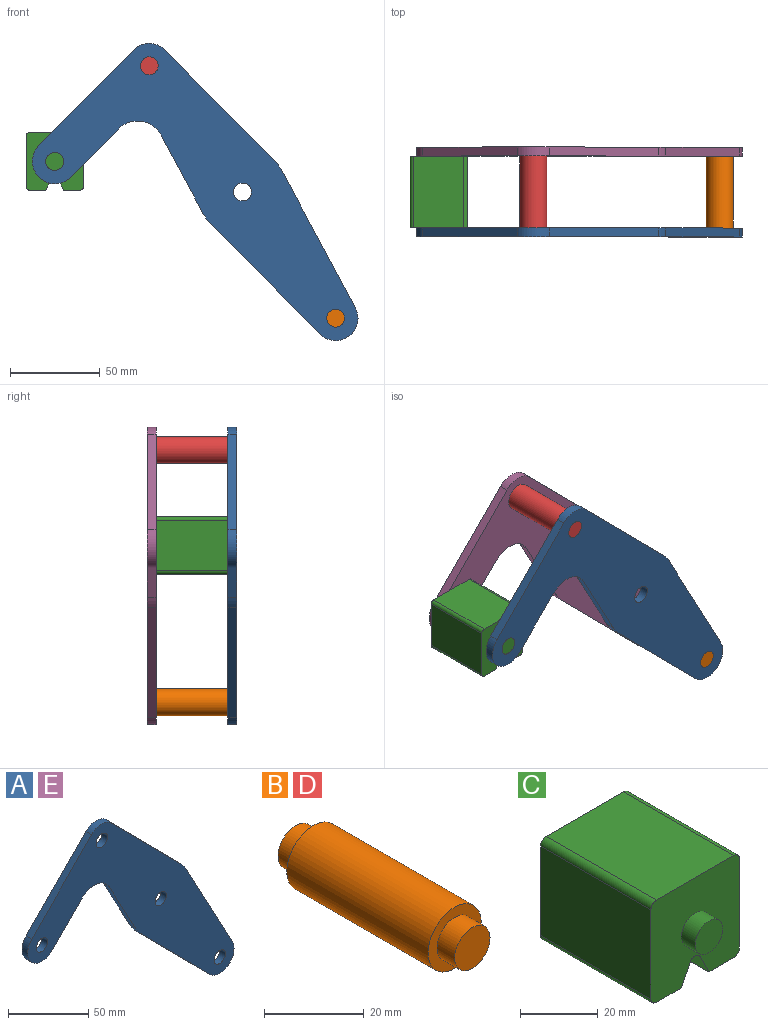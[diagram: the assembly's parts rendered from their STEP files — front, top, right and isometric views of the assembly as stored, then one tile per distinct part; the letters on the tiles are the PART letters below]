
ASSEMBLY  parts=5 mates=3
PART A: 18 faces, bbox 181.7x5x165.8 mm
  f0: plane 43.49x23.35mm, normal (-0.88,0,-0.47), area 246.8mm2, adj f1,f14,f16,f17
  f1: cylinder r=25mm len=5.75mm, axis (0,1,0), area 35.8mm2, adj f0,f2,f16,f17
  f2: plane 61.6x60.87mm, normal (-0.71,0,-0.7), area 433mm2, adj f1,f3,f16,f17
  f3: cylinder r=12.5mm len=21.39mm, axis (0,1,0), area 178.4mm2, adj f2,f4,f16,f17
  f4: plane 76.3x40.96mm, normal (0.88,0,0.47), area 433mm2, adj f3,f5,f16,f17
  f5: cylinder r=25mm len=5.75mm, axis (0,1,0), area 35.8mm2, adj f4,f6,f16,f17
  f6: plane 61.6x60.87mm, normal (0.71,0,0.7), area 433mm2, adj f5,f7,f16,f17
  f7: cylinder r=12.5mm len=17.78mm, axis (0,1,0), area 98.9mm2, adj f6,f8,f16,f17
  f8: plane 53.35x52.71mm, normal (-0.71,0,0.7), area 375mm2, adj f7,f9,f16,f17
  f9: cylinder r=12.5mm len=21.39mm, axis (0,1,0), area 196.3mm2, adj f8,f10,f16,f17
  f10: plane 26.86x26.54mm, normal (0.71,0,-0.7), area 188.8mm2, adj f9,f14,f16,f17
  f11: cylinder r=5mm len=10mm, axis (0,1,0), area 157.1mm2, adj f16,f17
  f12: cylinder r=5mm len=10mm, axis (0,1,0), area 157.1mm2, adj f16,f17
  f13: cylinder r=5mm len=10mm, axis (0,1,0), area 157.1mm2, adj f16,f17
  f14: cylinder r=15mm len=23.89mm, axis (0,1,0), area 140.2mm2, adj f0,f10,f16,f17
  f15: cylinder r=5mm len=10mm, axis (0,1,0), area 157.1mm2, adj f16,f17
  f16: plane 181.66x165.78mm, normal (0,-1,0), area 8710.1mm2, adj f0,f1,f2,f3,f4,f5,f6,f7
  f17: plane 181.66x165.78mm, normal (0,1,0), area 8710.1mm2, adj f0,f1,f2,f3,f4,f5,f6,f7
PART B: 7 faces, bbox 15x50x15 mm
  f0: cylinder r=7.5mm len=40mm, axis (0,-1,0), area 1885mm2, adj f2,f5
  f1: cylinder r=5mm len=10mm, axis (0,1,0), area 157.1mm2, adj f2,f3
  f2: plane 15x15mm, normal (0,-1,0), area 98.2mm2, adj f0,f1
  f3: plane 10x10mm, normal (0,-1,0), area 78.5mm2, adj f1
  f4: cylinder r=5mm len=10mm, axis (0,-1,0), area 157.1mm2, adj f5,f6
  f5: plane 15x15mm, normal (0,1,0), area 98.2mm2, adj f0,f4
  f6: plane 10x10mm, normal (0,1,0), area 78.5mm2, adj f4
PART C: 18 faces, bbox 32.1x50x32.1 mm
  f0: plane 40x28.08mm, normal (1,0,0), area 1123.1mm2, adj f4,f10,f13,f14
  f1: plane 40x9.04mm, normal (0,0,-1), area 361.6mm2, adj f2,f4,f10,f14
  f2: plane 40x6.42mm, normal (-0.89,0,-0.45), area 287.2mm2, adj f1,f4,f10,f15
  f3: plane 40x6.42mm, normal (0.89,0,-0.45), area 287.2mm2, adj f4,f5,f10,f15
  f4: plane 32.08x32.08mm, normal (0,-1,0), area 900.6mm2, adj f0,f1,f2,f3,f5,f6,f7,f9
  f5: plane 40x9.04mm, normal (0,0,-1), area 361.6mm2, adj f3,f4,f10,f16
  f6: plane 40x28.08mm, normal (0,0,1), area 1123.1mm2, adj f4,f10,f13,f17
  f7: plane 40x28.08mm, normal (-1,0,0), area 1123.1mm2, adj f4,f10,f16,f17
  f8: plane 10x10mm, normal (0,-1,0), area 78.5mm2, adj f9
  f9: cylinder r=5mm len=10mm, axis (0,1,0), area 157.1mm2, adj f4,f8
  f10: plane 32.08x32.08mm, normal (0,1,0), area 900.6mm2, adj f0,f1,f2,f3,f5,f6,f7,f12
  f11: plane 10x10mm, normal (0,1,0), area 78.5mm2, adj f12
  f12: cylinder r=5mm len=10mm, axis (0,-1,0), area 157.1mm2, adj f10,f11
  f13: cylinder r=2mm len=40mm, axis (0,1,0), area 125.7mm2, adj f0,f4,f6,f10
  f14: cylinder r=2mm len=40mm, axis (0,-1,0), area 125.7mm2, adj f0,f1,f4,f10
  f15: cylinder r=2mm len=40mm, axis (0,1,0), area 177.1mm2, adj f2,f3,f4,f10
  f16: cylinder r=2mm len=40mm, axis (0,1,0), area 125.7mm2, adj f4,f5,f7,f10
  f17: cylinder r=2mm len=40mm, axis (0,-1,0), area 125.7mm2, adj f4,f6,f7,f10
PART D: same geometry as B
PART E: same geometry as A
PLACE A t=(0,-20,0)mm fixed
PLACE B t=(103.95,-20,-140.78)mm
PLACE C t=(0,-20,0)mm
PLACE D t=(0,-20,0)mm
PLACE E t=(0,25,0)mm
MATE revolute C.f9 <-> A.f9  axis (0,-1,0) through (-104.69,-20,17.04)mm
MATE fastened E.f7 <-> D.f0  axis (0,-1,0) through (-51.98,20,70.39)mm
MATE fastened B.f0 <-> A.f3  axis (0,-1,0) through (51.98,-20,-70.39)mm
